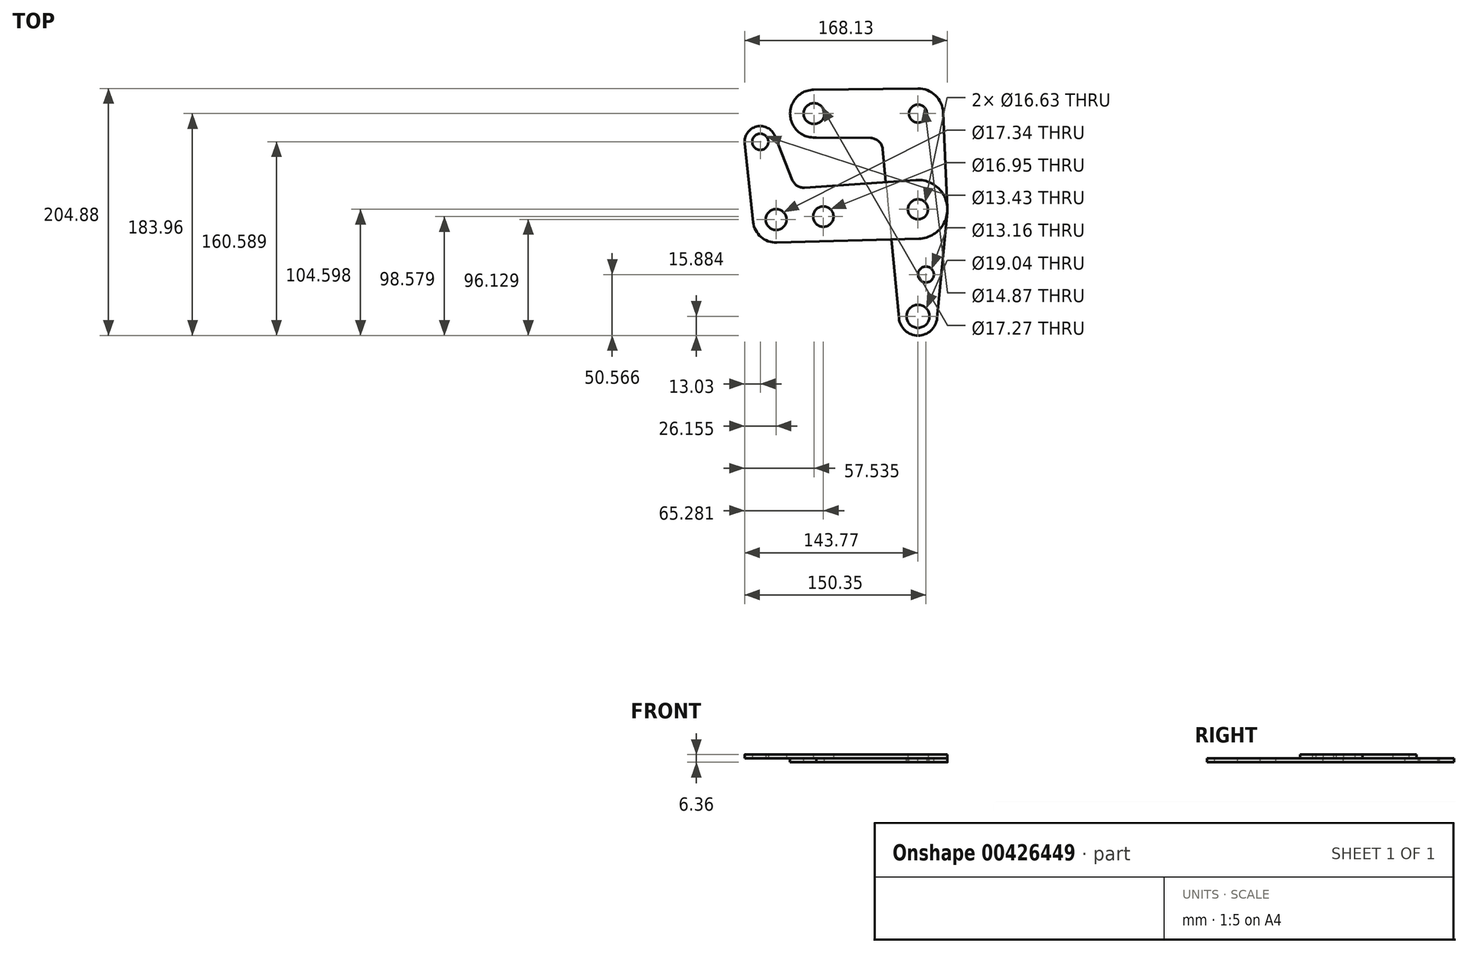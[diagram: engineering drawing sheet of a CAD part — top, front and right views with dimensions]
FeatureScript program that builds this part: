
annotation { "Feature Type Name" : "Feature", "Feature Type Description" : "" }
export const myFeature = defineFeature(function(context is Context, id is Id, definition is map)
    precondition{}
    {
        {
            var Q0;
            Q0=qCreatedBy(makeId("Top.planeOp"),FACE);
            var sketch = newSketch(context, id + "F0", { "sketchPlane" : qUnion([Q0])});
            skCircle(sketch, "E0", {"center": v(-61.99, 55) * mm, "radius": 8.63 * mm});
            skCircle(sketch, "E1", {"center": v(-61.99, 55) * mm, "radius": 19.8 * mm});
            skCircle(sketch, "E2", {"center": v(24.25, 55) * mm, "radius": 7.44 * mm});
            skCircle(sketch, "E3", {"center": v(24.25, 55) * mm, "radius": 20.92 * mm});
            skLineSegment(sketch, "E4", {"start": v(-62.24, 74.8) * mm, "end": v(23.98, 75.92) * mm});
            skCircle(sketch, "E5", {"center": v(24.25, -24.36) * mm, "radius": 8.32 * mm});
            skCircle(sketch, "E6", {"center": v(24.25, -24.36) * mm, "radius": 6.47 * mm});
            skCircle(sketch, "E7", {"center": v(24.25, -24.36) * mm, "radius": 24.36 * mm});
            skCircle(sketch, "E8", {"center": v(24.25, -113.08) * mm, "radius": 9.52 * mm});
            skCircle(sketch, "E9", {"center": v(24.25, -113.08) * mm, "radius": 15.88 * mm});
            skCircle(sketch, "E10", {"center": v(30.83, -78.4) * mm, "radius": 6.58 * mm});
            skCircle(sketch, "E11", {"center": v(-93.36, -32.83) * mm, "radius": 8.67 * mm});
            skCircle(sketch, "E12", {"center": v(-93.36, -32.83) * mm, "radius": 19.1 * mm});
            skCircle(sketch, "E13", {"center": v(-106.49, 31.63) * mm, "radius": 6.71 * mm});
            skCircle(sketch, "E14", {"center": v(-106.49, 31.63) * mm, "radius": 13.03 * mm});
            skLineSegment(sketch, "E15", {"start": v(45.15, 55.9) * mm, "end": v(48.59, -23.3) * mm});
            skLineSegment(sketch, "E16", {"start": v(48.5, -26.7) * mm, "end": v(40.06, -114.6) * mm});
            skLineSegment(sketch, "E17", {"start": v(0, -26.7) * mm, "end": v(8.44, -114.6) * mm});
            skArc(sketch, "E18", {"start": v(-5.02, 25.53) * mm, "mid": v(-8.25, 32.04) * mm, "end": v(-15, 34.72) * mm});
            skLineSegment(sketch, "E19", {"start": v(-15, 34.72) * mm, "end": v(-59.97, 35.3) * mm});
            skLineSegment(sketch, "E20", {"start": v(-5.02, 25.53) * mm, "end": v(0, -26.7) * mm});
            skCircle(sketch, "E21", {"center": v(-54.24, -30.38) * mm, "radius": 8.47 * mm});
            skLineSegment(sketch, "E22", {"start": v(-112.36, -34.9) * mm, "end": v(-119.45, 30.22) * mm});
            skLineSegment(sketch, "E23", {"start": v(-92.84, -51.93) * mm, "end": v(24.91, -48.71) * mm});
            skArc(sketch, "E24", {"start": v(-79.9, 0) * mm, "mid": v(-75.87, -4.84) * mm, "end": v(-69.76, -6.38) * mm});
            skLineSegment(sketch, "E25", {"start": v(-79.9, 0) * mm, "end": v(-94.38, 36.44) * mm});
            skLineSegment(sketch, "E26", {"start": v(-69.76, -6.38) * mm, "end": v(22.58, -0.06) * mm});
            skSolve(sketch);
        }
        {
            var Q0;
            Q0=makeQuery(id+"F0.imprint","IMPRINT",FACE,{"disambiguationData":[TD([[makeQuery(id+"F0.imprint","IMPRINT",EDGE,{"derivedFrom":sQuery(id+"F0.wireOp",EDGE,"E0")}),-1.0]])]});
            var Q1;
            Q1=makeQuery(id+"F0.imprint","IMPRINT",FACE,{"disambiguationData":[TD([[makeQuery(id+"F0.imprint","IMPRINT",EDGE,{"derivedFrom":sQuery(id+"F0.wireOp",EDGE,"E2")}),-1.0]])]});
            var Q2;
            Q2=makeQuery(id+"F0.imprint","IMPRINT",FACE,{"disambiguationData":[TD([[makeQuery(id+"F0.imprint","IMPRINT",EDGE,{"derivedFrom":sQuery(id+"F0.wireOp",EDGE,"E8")}),-1.0]])]});
            var Q3;
            {var subQ1=sQuery(id+"F0.wireOp",EDGE,"E7");var subQ3=sQuery(id+"F0.wireOp",EDGE,"E26");var subQ4=makeQuery(id+"F0.imprint","INTERSECT",VERTEX,{"derivedFrom":[subQ1,subQ3]});Q3=makeQuery(id+"F0.imprint","IMPRINT",FACE,{"disambiguationData":[TD([[makeQuery(id+"F0.imprint","IMPRINT",EDGE,{"disambiguationData":[TD([[subQ4,1.0]])],"derivedFrom":subQ3}),-1.0]])]});}
            var Q4;
            {var subQ1=sQuery(id+"F0.wireOp",EDGE,"E7");var subQ3=sQuery(id+"F0.wireOp",EDGE,"E23");var subQ4=makeQuery(id+"F0.imprint","INTERSECT",VERTEX,{"derivedFrom":[subQ1,subQ3]});Q4=makeQuery(id+"F0.imprint","IMPRINT",FACE,{"disambiguationData":[TD([[makeQuery(id+"F0.imprint","IMPRINT",EDGE,{"disambiguationData":[TD([[subQ4,1.0]])],"derivedFrom":subQ3}),1.0]])]});}
            var Q5;
            {var subQ4=sQuery(id+"F0.wireOp",EDGE,"E4");Q5=makeQuery(id+"F0.imprint","IMPRINT",FACE,{"disambiguationData":[TD([[makeQuery(id+"F0.imprint","IMPRINT",EDGE,{"derivedFrom":subQ4}),-1.0]])]});}
            var Q6;
            Q6=makeQuery(id+"F0.imprint","IMPRINT",FACE,{"disambiguationData":[TD([[makeQuery(id+"F0.imprint","IMPRINT",EDGE,{"derivedFrom":sQuery(id+"F0.wireOp",EDGE,"E10")}),-1.0]])]});
            var Q7;
            Q7=makeQuery(id+"F0.imprint","IMPRINT",FACE,{"disambiguationData":[TD([[makeQuery(id+"F0.imprint","IMPRINT",EDGE,{"derivedFrom":sQuery(id+"F0.wireOp",EDGE,"E5")}),-1.0]])]});
            extrude(context, id + "F1", {"entities" : qUnion([Q0, Q1, Q2, Q3, Q4, Q5, Q6, Q7]), "oppositeDirection" : true, "depth" : 3.17 * mm});
        }
        {
            var Q0;
            Q0=makeQuery(id+"F0.imprint","IMPRINT",FACE,{"disambiguationData":[TD([[makeQuery(id+"F0.imprint","IMPRINT",EDGE,{"derivedFrom":sQuery(id+"F0.wireOp",EDGE,"E13")}),-1.0]])]});
            var Q1;
            Q1=makeQuery(id+"F0.imprint","IMPRINT",FACE,{"disambiguationData":[TD([[makeQuery(id+"F0.imprint","IMPRINT",EDGE,{"derivedFrom":sQuery(id+"F0.wireOp",EDGE,"E21")}),-1.0]])]});
            var Q2;
            Q2=makeQuery(id+"F0.imprint","IMPRINT",FACE,{"disambiguationData":[TD([[makeQuery(id+"F0.imprint","IMPRINT",EDGE,{"derivedFrom":sQuery(id+"F0.wireOp",EDGE,"E11")}),-1.0]])]});
            var Q3;
            {var subQ1=sQuery(id+"F0.wireOp",EDGE,"E7");var subQ3=sQuery(id+"F0.wireOp",EDGE,"E26");var subQ4=makeQuery(id+"F0.imprint","INTERSECT",VERTEX,{"derivedFrom":[subQ1,subQ3]});Q3=makeQuery(id+"F0.imprint","IMPRINT",FACE,{"disambiguationData":[TD([[makeQuery(id+"F0.imprint","IMPRINT",EDGE,{"disambiguationData":[TD([[subQ4,1.0]])],"derivedFrom":subQ3}),-1.0]])]});}
            var Q4;
            {var subQ1=sQuery(id+"F0.wireOp",EDGE,"E7");var subQ3=sQuery(id+"F0.wireOp",EDGE,"E23");var subQ4=makeQuery(id+"F0.imprint","INTERSECT",VERTEX,{"derivedFrom":[subQ1,subQ3]});Q4=makeQuery(id+"F0.imprint","IMPRINT",FACE,{"disambiguationData":[TD([[makeQuery(id+"F0.imprint","IMPRINT",EDGE,{"disambiguationData":[TD([[subQ4,1.0]])],"derivedFrom":subQ3}),1.0]])]});}
            var Q5;
            Q5=makeQuery(id+"F0.imprint","IMPRINT",FACE,{"disambiguationData":[TD([[makeQuery(id+"F0.imprint","IMPRINT",EDGE,{"derivedFrom":sQuery(id+"F0.wireOp",EDGE,"E5")}),-1.0]])]});
            extrude(context, id + "F2", {"entities" : qUnion([Q0, Q1, Q2, Q3, Q4, Q5]), "depth" : 3.17 * mm});
        }
    });
